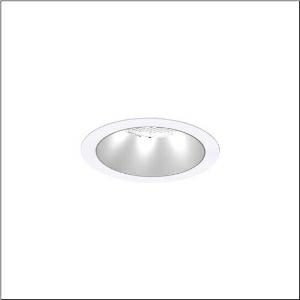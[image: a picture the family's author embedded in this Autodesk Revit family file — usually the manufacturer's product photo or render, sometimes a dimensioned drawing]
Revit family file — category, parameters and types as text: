
# Revit family: lunis_21_l_51db19ed91c
name_source: partatom
category: Lighting Fixtures
units: mm (PartAtom-declared; Revit-internal decimal feet)

## family parameters
Cut with Voids When Loaded = No
Host = Face
Light Source = No
Part Type = Normal
Room Calculation Point = No
Round Connector Dimension = Use Diameter
Shared = No

## types (1)
- --- (1 x LED, 3860 lm, 25.4 W, 6500K)
    Apparent Load = 25 VA
    CIE Flux Codes = 91 99 100 100 100
    Color Rendering = 80
    Color Temperature = 6500K
    Default Elevation = 1800 mm
    Description = Lunis 21,  L, downlight, light control with lens, of PMMA, anti glare with reflector, of PC, matt, light emission: direct distribution, LED rated luminous flux: 2.020lm, light colour: 830/840/865, with terminal, 5-pole, mains connection: 220..240V, AC/DC, 0/50..60Hz, housing, round, of diecast aluminium, traffic white (RAL 9016), diameter: 165mm, clamping range: 1..40mm, protection rating (complete): IP20, protection rating (on room side): IP54, insulation class (complete): insulation class II (safety insulation), certification: CE, impact resistance: IK03, packaging unit: 1 piece
    Height = 0 mm  [stored 0 ft]
    Lamp = 1 x LED
    Lamp Light Flux = 3860 lm
    Lamp Power = 25.4 W
    Lamp count = 1
    Length = 165 mm
    Luminous efficacy = 152 lm/W
    Manufacturer = Siteco
    ModVariant = No
    Model = 51DB19ED91C
    Mounting Place = Ceiling
    Mounting Type = Recessed
    Number of Poles = 1
    OnlyDefault = Yes
    Power Factor = 1
    Product Name = Lunis 21 L
    Product group = downlight
    ProductGroupID = 400
    Protection Class = Protection class II
    Protection Degree = IP 20
    RLX_Detail_Level = 1
    RLX_Emergency_Light_Flux = 0 lm
    RLX_Emergency_Type = 0
    RLX_Emergency_Type_DB = No
    RlxData = <blob elided: 18633 chars, md5=e984193a>
    Socket = socket
    Standby Power = 0 W
    System Light Flux = 3860 lm
    System Power = 25 W
    Type Comments = individual setting: colour temperature 6500K, luminous flux: 100 % | (ON | ON | OFF | OFF) | 700 mA
    Type Image = l_1291096.jpg
    URL = http://relux.com
    VarID = @adj_018870
    Voltage = 0 V
    Weight = 0.00 kg
    Width = 0 mm  [stored 0 ft]

note: [stored X ft] marks values corroborated as IEEE doubles in the binary element streams (Revit-internal decimal feet)

## geometry (parser evidence)
native form markers: Blend x4, Sweep x11
no freeform markers — native parametric forms only
